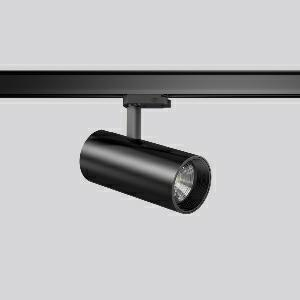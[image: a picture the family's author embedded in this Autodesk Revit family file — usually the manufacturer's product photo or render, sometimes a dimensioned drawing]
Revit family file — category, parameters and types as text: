
# Revit family: deecos_s_mini_742194_003_76_9421
name_source: partatom
category: Lighting Fixtures
units: mm (PartAtom-declared; Revit-internal decimal feet)

## family parameters
Cut with Voids When Loaded = No
Host = Face
Light Source = No
Part Type = Normal
Room Calculation Point = No
Round Connector Dimension = Use Diameter
Shared = No

## types (1)
- DEECOS S mini (1 x LED Modul 930, 2000 lm, 3000)
    Apparent Load = 22 VA
    Approval mark = CE
    CIE Flux Codes = 99 100 100 100 100
    Color Rendering = 90
    Color Temperature = 3000
    Default Elevation = 1800 mm
    Description = Series: DEECOS S mini
LED surface-mounted projector in modern design with no visible cooling ribs. Housing: die-cast aluminium, powder-coated. Rotation range: 356°. Swivel range: 90°. Black plastic ring and recessed LED to prevent glare from the side. Optical assembly with lens made of plastic (polycarbonate) for the best homogeneous light distribution - can be changed without tools. Best colour rendering index Ra>90. Superspot version with small spot LED. With adapter for RZB 3-circuit DALI tracks. Suitable for Track on ceiling, Wall track. High quality converter without flickering and stroboscopic effect. The following accessories can be mounted without use of tools: interchangeable lenses, decorative glasses, honeycomb louvre, clear and frosted diffusers, white interchangeable plastic ring. 
Colour: deep black, matt (RAL 9005)
Diameter: 87 mm
Height: 214 mm
Lamp: LED
Socket: without socket
Colour temperature: 3000K
Colour rendering index (CRI): 92
System power: 22 W
Rated luminous flux: 2000 lm
Luminous efficiency: 91 lm/W
Control gear: Converter, dimmable, DALI
Protection class: I
Type of protection: IP 20
    Height = 214 mm
    Lamp = 1 x LED Modul 930
    Lamp Light Flux = 2000 lm
    Lamp count = 1
    Length = 87 mm
    Lifetime = 50000 h
    Luminous efficacy = 91 lm/W
    Manufacturer = RZB
    ModVariant = No
    Model = 742194.003.76
    Mounting Place = Ceiling
    Mounting Type = Rail mounted
    Number of Poles = 1
    OnlyDefault = Yes
    Power Factor = 1
    Product Name = DEECOS S mini
    Product group = Track mounted projectors
    ProductGroupID = 301
    Protection Class = Protection class I
    Protection Degree = IP 20
    RLX_Detail_Level = 1
    RLX_Emergency_Light_Flux = 0 lm
    RLX_Emergency_Type = 0
    RLX_Emergency_Type_DB = No
    RlxData = <blob elided: 38617 chars, md5=fb27b3cd>
    Socket = socket
    Standby Power = 0 W
    System Light Flux = 2000 lm
    System Power = 22 W
    Type Comments = Product without accessories
    Type Image = 741930.003.jpg
    URL = http://relux.com
    VarID = ---
    Voltage = 230 V
    Voltage Range = 220-240 V
    Weight = 0.00 kg
    Width = 0 mm  [stored 0 ft]

note: [stored X ft] marks values corroborated as IEEE doubles in the binary element streams (Revit-internal decimal feet)

## geometry (parser evidence)
native form markers: Blend x4, Sweep x12
no freeform markers — native parametric forms only
